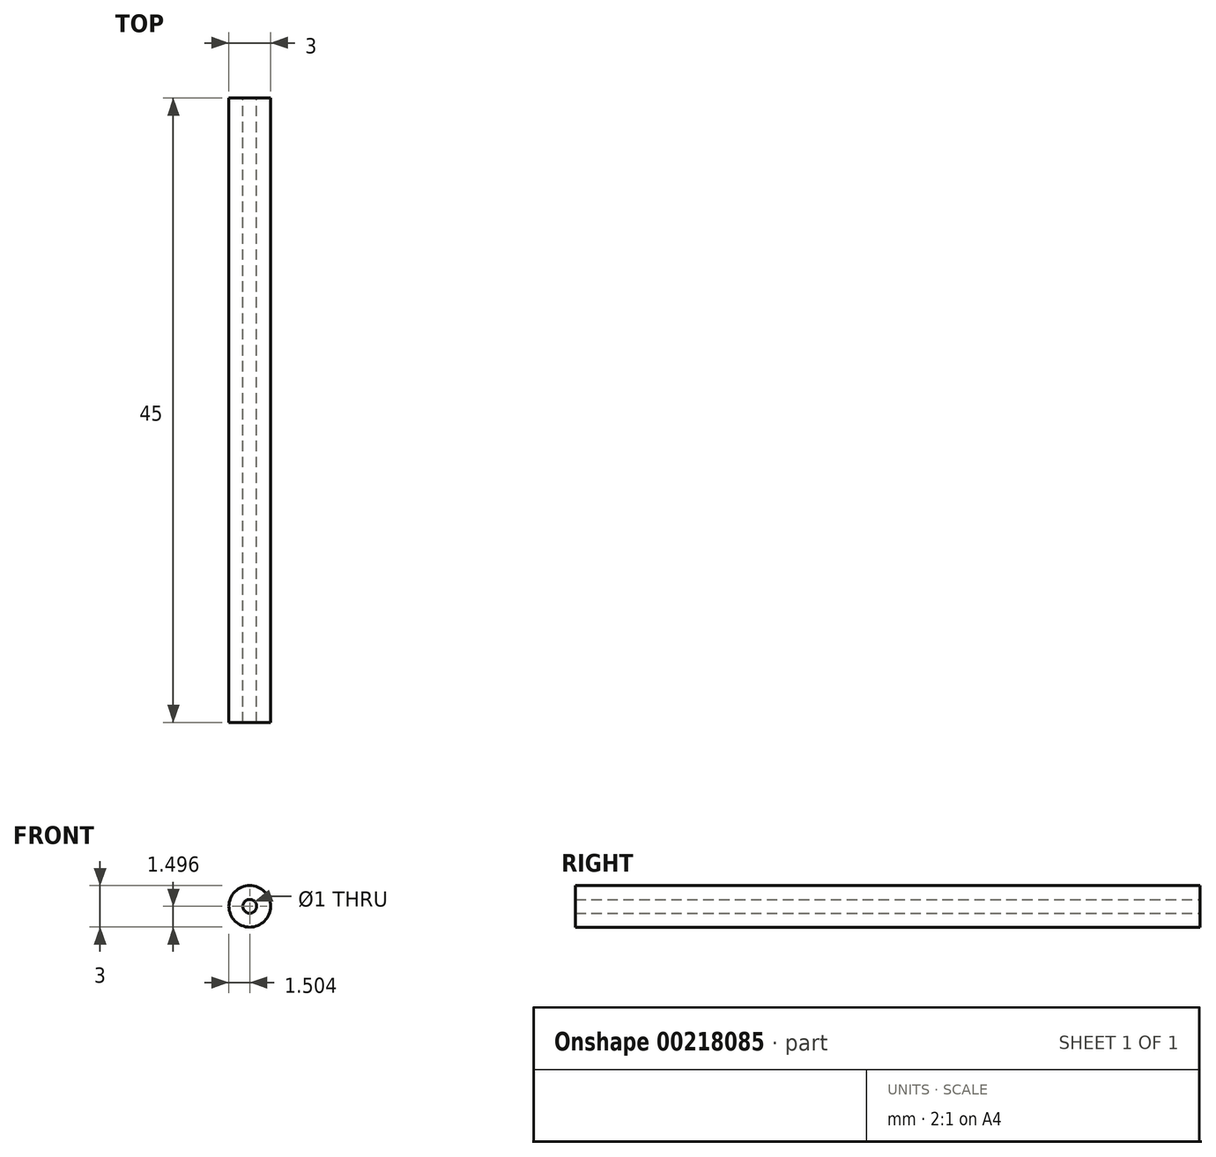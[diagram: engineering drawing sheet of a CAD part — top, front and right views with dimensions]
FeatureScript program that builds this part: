
annotation { "Feature Type Name" : "Feature", "Feature Type Description" : "" }
export const myFeature = defineFeature(function(context is Context, id is Id, definition is map)
    precondition{}
    {
        {
            var Q0;
            Q0=qCreatedBy(makeId("Front.planeOp"),FACE);
            var sketch = newSketch(context, id + "F0", { "sketchPlane" : qUnion([Q0])});
            skCircle(sketch, "E0", {"center": v(18.68, 12.5) * mm, "radius": 1.5 * mm});
            skCircle(sketch, "E1", {"center": v(18.68, 12.5) * mm, "radius": 0.5 * mm});
            skSolve(sketch);
        }
        {
            var Q0;
            Q0=makeQuery(id+"F0.imprint","IMPRINT",FACE,{"disambiguationData":[TD([[makeQuery(id+"F0.imprint","IMPRINT",EDGE,{"derivedFrom":sQuery(id+"F0.wireOp",EDGE,"E0")}),1.0]])]});
            extrude(context, id + "F1", {"entities" : qUnion([Q0]), "depth" : 45 * mm});
        }
    });
